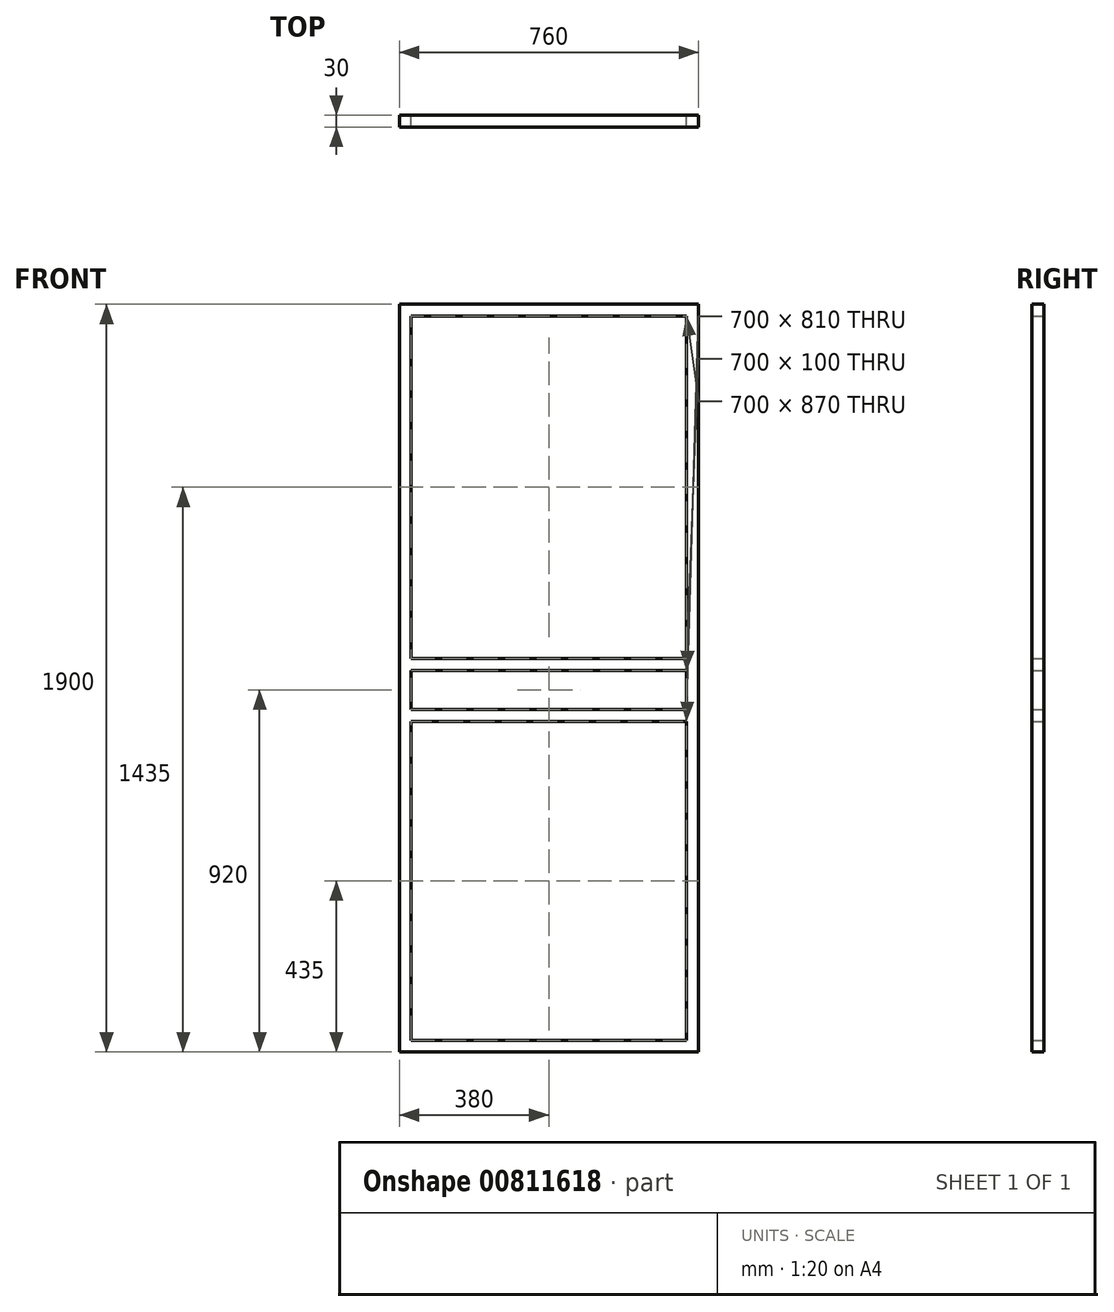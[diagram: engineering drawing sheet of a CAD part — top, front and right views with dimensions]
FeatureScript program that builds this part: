
annotation { "Feature Type Name" : "Feature", "Feature Type Description" : "" }
export const myFeature = defineFeature(function(context is Context, id is Id, definition is map)
    precondition{}
    {
        {
            var Q0;
            Q0=qCreatedBy(makeId("Front.planeOp"),FACE);
            var sketch = newSketch(context, id + "F0", { "sketchPlane" : qUnion([Q0])});
            skLineSegment(sketch, "E0.top", {"start": v(380, -900) * mm, "end": v(-380, -900) * mm});
            skLineSegment(sketch, "E0.left", {"start": v(380, 900) * mm, "end": v(380, -900) * mm});
            skLineSegment(sketch, "E0.right", {"start": v(-380, 900) * mm, "end": v(-380, -900) * mm});
            skPoint(sketch, "E0.middle", {"position": v(0, 0) * mm});
            skLineSegment(sketch, "E1.1", {"start": v(350, 870) * mm, "end": v(350, 100) * mm});
            skLineSegment(sketch, "E1.2", {"start": v(350, -870) * mm, "end": v(-350, -870) * mm});
            skLineSegment(sketch, "E1.3", {"start": v(-350, 870) * mm, "end": v(-350, 100) * mm});
            skLineSegment(sketch, "E2", {"start": v(0, -900) * mm, "end": v(0, 100) * mm, "construction": true});
            skPoint(sketch, "E2.endSnap0", {"position": v(0, -900) * mm});
            skLineSegment(sketch, "E3.bottom", {"start": v(-350, 100) * mm, "end": v(350, 100) * mm});
            skLineSegment(sketch, "E3.top", {"start": v(-350, 70) * mm, "end": v(350, 70) * mm});
            skLineSegment(sketch, "E4", {"start": v(-170.97, 70) * mm, "end": v(-170.97, -30) * mm, "construction": true});
            skLineSegment(sketch, "E5.bottom", {"start": v(-350, -30) * mm, "end": v(350, -30) * mm});
            skLineSegment(sketch, "E5.top", {"start": v(-350, -60) * mm, "end": v(350, -60) * mm});
            skLineSegment(sketch, "E6.trimOffspring", {"start": v(-350, 70) * mm, "end": v(-350, -30) * mm});
            skPoint(sketch, "E3.left.start.orphan", {"position": v(-368.05, 100) * mm});
            skLineSegment(sketch, "E7.trimOffspring", {"start": v(-350, -60) * mm, "end": v(-350, -870) * mm});
            skPoint(sketch, "E5.left.start.orphan", {"position": v(-366.7, -30) * mm});
            skLineSegment(sketch, "E8.trimOffspring", {"start": v(350, -60) * mm, "end": v(350, -870) * mm});
            skLineSegment(sketch, "E9.trimOffspring", {"start": v(350, 70) * mm, "end": v(350, -30) * mm});
            skLineSegment(sketch, "E10", {"start": v(380, 900) * mm, "end": v(380, 1000) * mm});
            skLineSegment(sketch, "E11", {"start": v(380, 1000) * mm, "end": v(-380, 1000) * mm});
            skLineSegment(sketch, "E12", {"start": v(-380, 1000) * mm, "end": v(-380, 900) * mm});
            skLineSegment(sketch, "E13", {"start": v(350, 870) * mm, "end": v(350, 970) * mm});
            skLineSegment(sketch, "E14", {"start": v(-350, 870) * mm, "end": v(-350, 970) * mm});
            skPoint(sketch, "E15.endSnap0", {"position": v(0, 1000) * mm});
            skLineSegment(sketch, "E16", {"start": v(350, 970) * mm, "end": v(-350, 970) * mm});
            skPoint(sketch, "E15.end.orphan", {"position": v(0, 970) * mm});
            skPoint(sketch, "E15.start.orphan", {"position": v(0, 1000) * mm});
            skSolve(sketch);
        }
        {
            var Q0;
            Q0=qSketchRegion(id+"F0",true);
            extrude(context, id + "F1", {"entities" : qUnion([Q0]), "depth" : 30 * mm});
        }
    });
